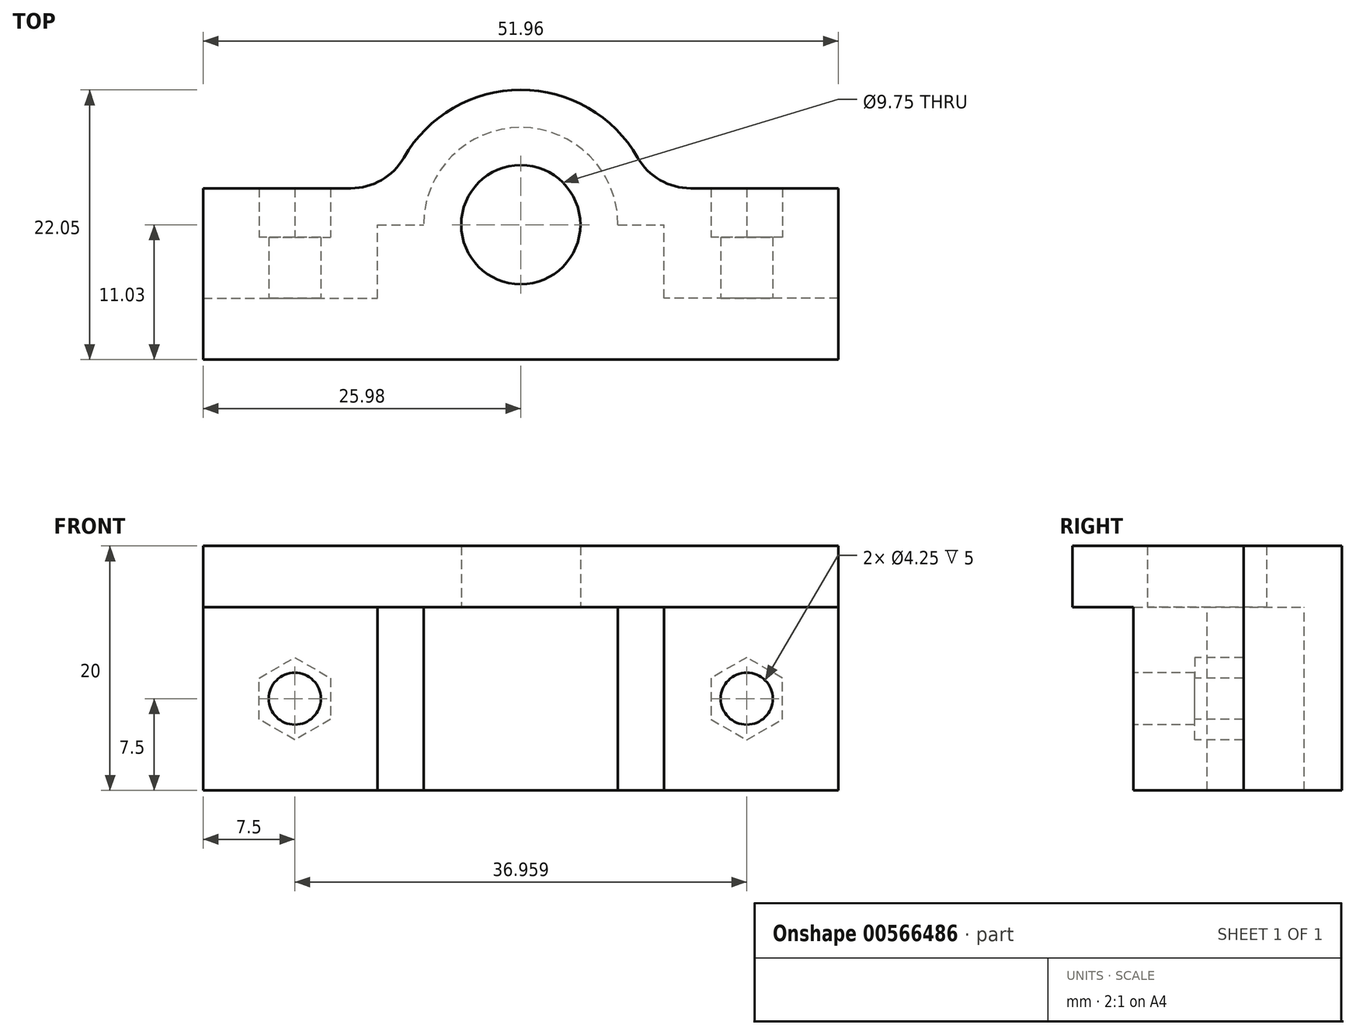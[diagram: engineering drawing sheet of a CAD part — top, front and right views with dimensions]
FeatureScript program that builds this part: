
annotation { "Feature Type Name" : "Feature", "Feature Type Description" : "" }
export const myFeature = defineFeature(function(context is Context, id is Id, definition is map)
    precondition{}
    {
        {
            var Q0;
            Q0=qCreatedBy(makeId("Top.planeOp"),FACE);
            var sketch = newSketch(context, id + "F0", { "sketchPlane" : qUnion([Q0])});
            skCircle(sketch, "E0", {"center": v(0, 0) * mm, "radius": 4.75 * mm});
            skCircle(sketch, "E1", {"center": v(0, 0) * mm, "radius": 7.83 * mm, "construction": true});
            skLineSegment(sketch, "E2", {"start": v(0, -11.03) * mm, "end": v(10.98, -11.03) * mm});
            skLineSegment(sketch, "E3", {"start": v(25.98, -11.03) * mm, "end": v(25.98, -6.02) * mm, "construction": true});
            skLineSegment(sketch, "E4", {"start": v(25.98, -6.02) * mm, "end": v(10.98, -6.03) * mm});
            skLineSegment(sketch, "E5", {"start": v(10.98, -1.03) * mm, "end": v(10.98, 1) * mm});
            skArc(sketch, "E6", {"start": v(10.98, 1) * mm, "mid": v(7.43, 8.14) * mm, "end": v(0, 11.03) * mm});
            skArc(sketch, "E7.MirrorCS", {"start": v(-10.98, 1) * mm, "mid": v(-7.43, 8.14) * mm, "end": v(0, 11.03) * mm});
            skLineSegment(sketch, "E8.MirrorCS", {"start": v(-10.98, -1.02) * mm, "end": v(-10.98, 1) * mm});
            skLineSegment(sketch, "E9.MirrorCS", {"start": v(-25.98, -6.02) * mm, "end": v(-10.98, -6.03) * mm});
            skLineSegment(sketch, "E10.MirrorCS", {"start": v(-25.98, -11.03) * mm, "end": v(-25.98, -6.02) * mm, "construction": true});
            skLineSegment(sketch, "E11.MirrorCS", {"start": v(0, -11.03) * mm, "end": v(-10.98, -11.03) * mm});
            skLineSegment(sketch, "E12", {"start": v(25.98, -6.02) * mm, "end": v(25.98, -1.02) * mm});
            skLineSegment(sketch, "E13", {"start": v(25.98, -1.02) * mm, "end": v(10.98, -1.03) * mm});
            skPoint(sketch, "E13.endSnap0", {"position": v(10.98, -2.51) * mm});
            skLineSegment(sketch, "E14.MirrorCS", {"start": v(-25.98, -1.02) * mm, "end": v(-10.98, -1.03) * mm});
            skLineSegment(sketch, "E15.MirrorCS", {"start": v(-25.98, -6.02) * mm, "end": v(-25.98, -1.02) * mm});
            skPoint(sketch, "E16.orphan", {"position": v(-10.98, -6.03) * mm});
            skLineSegment(sketch, "E17", {"start": v(-10.98, -11.03) * mm, "end": v(-10.98, -6.03) * mm});
            skLineSegment(sketch, "E18.MirrorCS", {"start": v(10.98, -11.03) * mm, "end": v(10.98, -6.03) * mm});
            skPoint(sketch, "E19.orphan", {"position": v(-25.98, -11.03) * mm});
            skSolve(sketch);
        }
        {
            var Q0;
            Q0=qSketchRegion(id+"F0",true);
            extrude(context, id + "F1", {"entities" : qUnion([Q0]), "endBound" : BoundingType.SYMMETRIC, "depth" : 15 * mm});
        }
        {
            var Q0;
            Q0=makeQuery(id+"F1.opExtrude","SWEPT_FACE",FACE,{"disambiguationData":[OSD([sQuery(id+"F0.wireOp",EDGE,"E2"),sQuery(id+"F0.wireOp",EDGE,"E11.MirrorCS")])]});
            var sketch = newSketch(context, id + "F2", { "sketchPlane" : qUnion([Q0])});
            skCircle(sketch, "E20", {"center": v(-18.48, 0) * mm, "radius": 2.12 * mm});
            skCircle(sketch, "E21.MirrorC", {"center": v(18.48, 0) * mm, "radius": 2.12 * mm});
            skSolve(sketch);
        }
        {
            var Q0;
            Q0=qSketchRegion(id+"F2",true);
            extrude(context, id + "F3", {"entities" : qUnion([Q0]), "operationType" : NewBodyOperationType.REMOVE, "oppositeDirection" : true, "depth" : 25 * mm});
        }
        {
            var Q0;
            Q0=makeQuery(id+"F1.opExtrude","CAP_FACE",FACE,{"disambiguationData":[OSD([sQuery(id+"F0.wireOp",EDGE,"E0"),sQuery(id+"F0.wireOp",EDGE,"E2"),sQuery(id+"F0.wireOp",EDGE,"E3"),sQuery(id+"F0.wireOp",EDGE,"E4"),sQuery(id+"F0.wireOp",EDGE,"E5"),sQuery(id+"F0.wireOp",EDGE,"E6"),sQuery(id+"F0.wireOp",EDGE,"E7.MirrorCS"),sQuery(id+"F0.wireOp",EDGE,"E8.MirrorCS"),sQuery(id+"F0.wireOp",EDGE,"E9.MirrorCS"),sQuery(id+"F0.wireOp",EDGE,"E10.MirrorCS"),sQuery(id+"F0.wireOp",EDGE,"E11.MirrorCS")])],"isStart":false});
            var sketch = newSketch(context, id + "F4", { "sketchPlane" : qUnion([Q0])});
            skArc(sketch, "E22", {"start": v(7.82, -0.01) * mm, "mid": v(0, 7.83) * mm, "end": v(-7.82, -0.01) * mm});
            skLineSegment(sketch, "E23.top", {"start": v(-10.98, -11.03) * mm, "end": v(10.98, -11.03) * mm});
            skLineSegment(sketch, "E23.left", {"start": v(-10.98, -6.03) * mm, "end": v(-10.98, -11.03) * mm});
            skLineSegment(sketch, "E23.right", {"start": v(10.98, -6.03) * mm, "end": v(10.98, -11.03) * mm});
            skPoint(sketch, "E24.startSnap0", {"position": v(-10.98, -0.01) * mm});
            skLineSegment(sketch, "E25", {"start": v(-7.82, -0.01) * mm, "end": v(-10.98, -0.01) * mm});
            skLineSegment(sketch, "E26", {"start": v(-10.98, -6.03) * mm, "end": v(-10.98, -0.01) * mm});
            skLineSegment(sketch, "E27.MirrorCS", {"start": v(7.82, -0.01) * mm, "end": v(10.98, -0.01) * mm});
            skLineSegment(sketch, "E28.MirrorCS", {"start": v(10.98, -6.03) * mm, "end": v(10.98, -0.01) * mm});
            skPoint(sketch, "E23.bottom.end.orphan", {"position": v(-7.82, -6.03) * mm});
            skPoint(sketch, "E29.trimOffspring.start.orphan", {"position": v(7.82, -6.03) * mm});
            skSolve(sketch);
        }
        {
            var Q0;
            Q0=qSketchRegion(id+"F4",true);
            extrude(context, id + "F5", {"entities" : qUnion([Q0]), "operationType" : NewBodyOperationType.REMOVE, "endBound" : BoundingType.THROUGH_ALL, "oppositeDirection" : true, "depth" : 10 * mm});
        }
        {
            var Q0;
            Q0=qCreatedBy(makeId("Top.planeOp"),FACE);
            var sketch = newSketch(context, id + "F6", { "sketchPlane" : qUnion([Q0])});
            skLineSegment(sketch, "E30", {"start": v(-10.98, 1) * mm, "end": v(-10.98, -1.03) * mm});
            skLineSegment(sketch, "E31", {"start": v(-10.98, -1.03) * mm, "end": v(-14.18, -1.03) * mm});
            skLineSegment(sketch, "E32", {"start": v(-14.18, -1.03) * mm, "end": v(-14.18, 2.97) * mm});
            skLineSegment(sketch, "E33", {"start": v(-14.18, 2.97) * mm, "end": v(-10.62, 2.97) * mm});
            skArc(sketch, "E34", {"start": v(-10.62, 2.98) * mm, "mid": v(-10.84, 2) * mm, "end": v(-10.98, 1) * mm});
            skArc(sketch, "E35.MirrorCS", {"start": v(10.62, 2.98) * mm, "mid": v(10.84, 2) * mm, "end": v(10.98, 1) * mm});
            skLineSegment(sketch, "E36.MirrorCS", {"start": v(10.98, -1.03) * mm, "end": v(14.18, -1.03) * mm});
            skLineSegment(sketch, "E37.MirrorCS", {"start": v(14.18, 2.98) * mm, "end": v(10.62, 2.97) * mm});
            skLineSegment(sketch, "E38.MirrorCS", {"start": v(10.98, 1) * mm, "end": v(10.98, -1.03) * mm});
            skLineSegment(sketch, "E39.MirrorCS", {"start": v(14.18, -1.03) * mm, "end": v(14.18, 2.97) * mm});
            skSolve(sketch);
        }
        {
            var Q0;
            Q0=qSketchRegion(id+"F6",true);
            extrude(context, id + "F7", {"entities" : qUnion([Q0]), "operationType" : NewBodyOperationType.ADD, "endBound" : BoundingType.SYMMETRIC, "depth" : 15 * mm});
        }
        {
            var Q0;
            {var subQ0=sQuery(id+"F0.wireOp",EDGE,"E9.MirrorCS");var subQ1=sQuery(id+"F0.wireOp",EDGE,"E14.MirrorCS");var subQ2=sQuery(id+"F0.wireOp",EDGE,"E15.MirrorCS");var subQ3=sQuery(id+"F0.wireOp",EDGE,"E13");var subQ4=sQuery(id+"F0.wireOp",EDGE,"E12");var subQ5=sQuery(id+"F0.wireOp",EDGE,"E8.MirrorCS");var subQ6=sQuery(id+"F0.wireOp",EDGE,"E7.MirrorCS");var subQ7=sQuery(id+"F0.wireOp",EDGE,"E6");var subQ8=sQuery(id+"F0.wireOp",EDGE,"E5");var subQ9=sQuery(id+"F0.wireOp",EDGE,"E4");var subQ10=makeQuery(id+"F1.opExtrude","CAP_FACE",FACE,{"disambiguationData":[OSD([sQuery(id+"F0.wireOp",EDGE,"E0"),sQuery(id+"F0.wireOp",EDGE,"E2"),subQ9,subQ8,subQ7,subQ6,subQ5,subQ0,sQuery(id+"F0.wireOp",EDGE,"E11.MirrorCS"),subQ4,subQ3,subQ1,subQ2,sQuery(id+"F0.wireOp",EDGE,"E17"),sQuery(id+"F0.wireOp",EDGE,"E18.MirrorCS")])],"isStart":false});Q0=makeQuery(id+"F7.boolean.opBoolean","MERGE",FACE,{"derivedFrom":[makeQuery(id+"F5.boolean.opBoolean","SPLIT",FACE,{"disambiguationData":[TD([makeQuery(id+"F1.opExtrude","SWEPT_FACE",FACE,{"disambiguationData":[OSD([subQ9])]})])],"derivedFrom":subQ10}),makeQuery(id+"F5.boolean.opBoolean","SPLIT",FACE,{"disambiguationData":[TD([makeQuery(id+"F1.opExtrude","SWEPT_FACE",FACE,{"disambiguationData":[OSD([subQ8])]})])],"derivedFrom":subQ10}),makeQuery(id+"F5.boolean.opBoolean","SPLIT",FACE,{"disambiguationData":[TD([makeQuery(id+"F1.opExtrude","SWEPT_FACE",FACE,{"disambiguationData":[OSD([subQ0])]})])],"derivedFrom":subQ10}),makeQuery(id+"F7.opExtrude","CAP_FACE",FACE,{"disambiguationData":[OSD([sQuery(id+"F6.wireOp",EDGE,"E30"),sQuery(id+"F6.wireOp",EDGE,"E31"),sQuery(id+"F6.wireOp",EDGE,"E32"),sQuery(id+"F6.wireOp",EDGE,"E33"),sQuery(id+"F6.wireOp",EDGE,"E34")])],"isStart":false}),makeQuery(id+"F7.opExtrude","CAP_FACE",FACE,{"disambiguationData":[OSD([sQuery(id+"F6.wireOp",EDGE,"E35.MirrorCS"),sQuery(id+"F6.wireOp",EDGE,"E36.MirrorCS"),sQuery(id+"F6.wireOp",EDGE,"E37.MirrorCS"),sQuery(id+"F6.wireOp",EDGE,"E38.MirrorCS"),sQuery(id+"F6.wireOp",EDGE,"E39.MirrorCS")])],"isStart":false})]});}
            var sketch = newSketch(context, id + "F8", { "sketchPlane" : qUnion([Q0])});
            skLineSegment(sketch, "E40", {"start": v(-10.98, -6.02) * mm, "end": v(-25.98, -6.02) * mm});
            skLineSegment(sketch, "E41", {"start": v(-25.98, -6.02) * mm, "end": v(-25.98, -1.02) * mm});
            skLineSegment(sketch, "E42", {"start": v(-25.98, -1.02) * mm, "end": v(-14.18, -1.03) * mm});
            skLineSegment(sketch, "E43", {"start": v(-14.18, -1.03) * mm, "end": v(-14.18, 2.98) * mm});
            skLineSegment(sketch, "E44", {"start": v(-14.18, 2.97) * mm, "end": v(-10.62, 2.97) * mm});
            skArc(sketch, "E45", {"start": v(-10.62, 2.97) * mm, "mid": v(0, 11.03) * mm, "end": v(10.62, 2.98) * mm});
            skLineSegment(sketch, "E46.MirrorCS", {"start": v(14.18, 2.98) * mm, "end": v(10.62, 2.98) * mm});
            skLineSegment(sketch, "E47.MirrorCS", {"start": v(14.18, -1.03) * mm, "end": v(14.18, 2.98) * mm});
            skLineSegment(sketch, "E48.MirrorCS", {"start": v(25.98, -1.02) * mm, "end": v(14.18, -1.03) * mm});
            skLineSegment(sketch, "E49.MirrorCS", {"start": v(25.98, -6.02) * mm, "end": v(25.98, -1.02) * mm});
            skLineSegment(sketch, "E50.MirrorCS", {"start": v(10.98, -6.02) * mm, "end": v(25.98, -6.02) * mm});
            skLineSegment(sketch, "E51", {"start": v(-10.98, -6.02) * mm, "end": v(10.98, -6.02) * mm});
            skCircle(sketch, "E52", {"center": v(0, 0) * mm, "radius": 4.88 * mm});
            skSolve(sketch);
        }
        {
            var Q0;
            Q0=qSketchRegion(id+"F8",true);
            extrude(context, id + "F9", {"entities" : qUnion([Q0]), "operationType" : NewBodyOperationType.ADD, "depth" : 5 * mm});
        }
        {
            var Q0;
            Q0=makeQuery(id+"F9.boolean.opBoolean","MERGE",FACE,{"derivedFrom":[makeQuery(id+"F1.opExtrude","SWEPT_FACE",FACE,{"disambiguationData":[OSD([sQuery(id+"F0.wireOp",EDGE,"E4")])]}),makeQuery(id+"F1.opExtrude","SWEPT_FACE",FACE,{"disambiguationData":[OSD([sQuery(id+"F0.wireOp",EDGE,"E9.MirrorCS")])]}),makeQuery(id+"F9.opExtrude","SWEPT_FACE",FACE,{"disambiguationData":[OSD([sQuery(id+"F8.wireOp",EDGE,"E40"),sQuery(id+"F8.wireOp",EDGE,"E50.MirrorCS"),sQuery(id+"F8.wireOp",EDGE,"E51")])]})]});
            var sketch = newSketch(context, id + "F10", { "sketchPlane" : qUnion([Q0])});
            skLineSegment(sketch, "E53.bottom", {"start": v(-25.98, 12.5) * mm, "end": v(25.98, 12.5) * mm});
            skLineSegment(sketch, "E53.top", {"start": v(-25.98, 7.5) * mm, "end": v(25.98, 7.5) * mm});
            skLineSegment(sketch, "E53.left", {"start": v(-25.98, 12.5) * mm, "end": v(-25.98, 7.5) * mm});
            skLineSegment(sketch, "E53.right", {"start": v(25.98, 12.5) * mm, "end": v(25.98, 7.5) * mm});
            skSolve(sketch);
        }
        {
            var Q0;
            Q0=qSketchRegion(id+"F10",true);
            extrude(context, id + "F11", {"entities" : qUnion([Q0]), "operationType" : NewBodyOperationType.ADD, "depth" : 5 * mm});
        }
        {
            var Q0;
            Q0=makeQuery(id+"F9.boolean.opBoolean","MERGE",FACE,{"derivedFrom":[makeQuery(id+"F1.opExtrude","SWEPT_FACE",FACE,{"disambiguationData":[OSD([sQuery(id+"F0.wireOp",EDGE,"E13")])]}),makeQuery(id+"F9.opExtrude","SWEPT_FACE",FACE,{"disambiguationData":[OSD([sQuery(id+"F8.wireOp",EDGE,"E48.MirrorCS")])]})]});
            var sketch = newSketch(context, id + "F12", { "sketchPlane" : qUnion([Q0])});
            skCircle(sketch, "E54.cCircle", {"center": v(-18.48, 0) * mm, "radius": 2.93 * mm, "construction": true});
            skLineSegment(sketch, "E54.0", {"start": v(-15.55, 1.69) * mm, "end": v(-15.55, -1.69) * mm});
            skLineSegment(sketch, "E54.1", {"start": v(-15.55, -1.69) * mm, "end": v(-18.48, -3.38) * mm});
            skLineSegment(sketch, "E54.2", {"start": v(-18.48, -3.38) * mm, "end": v(-21.4, -1.69) * mm});
            skLineSegment(sketch, "E54.3", {"start": v(-21.4, -1.69) * mm, "end": v(-21.4, 1.69) * mm});
            skLineSegment(sketch, "E54.4", {"start": v(-21.4, 1.69) * mm, "end": v(-18.48, 3.38) * mm});
            skLineSegment(sketch, "E54.5", {"start": v(-18.48, 3.38) * mm, "end": v(-15.55, 1.69) * mm});
            skPoint(sketch, "E54.0.midPoint", {"position": v(-15.55, 0) * mm});
            skLineSegment(sketch, "E55.MirrorCS", {"start": v(18.48, 3.38) * mm, "end": v(15.55, 1.69) * mm});
            skLineSegment(sketch, "E56.MirrorCS", {"start": v(21.4, 1.69) * mm, "end": v(18.48, 3.38) * mm});
            skLineSegment(sketch, "E57.MirrorCS", {"start": v(21.4, -1.69) * mm, "end": v(21.4, 1.69) * mm});
            skLineSegment(sketch, "E58.MirrorCS", {"start": v(18.48, -3.38) * mm, "end": v(21.4, -1.69) * mm});
            skLineSegment(sketch, "E59.MirrorCS", {"start": v(15.55, -1.69) * mm, "end": v(18.48, -3.38) * mm});
            skLineSegment(sketch, "E60.MirrorCS", {"start": v(15.55, 1.69) * mm, "end": v(15.55, -1.69) * mm});
            skPoint(sketch, "E61.MirrorP", {"position": v(15.55, 0) * mm});
            skCircle(sketch, "E62.MirrorC", {"center": v(18.48, 0) * mm, "radius": 2.93 * mm, "construction": true});
            skLineSegment(sketch, "E63.bottom", {"start": v(-25.98, 12.5) * mm, "end": v(-14.18, 12.5) * mm});
            skLineSegment(sketch, "E63.top", {"start": v(-25.98, -7.5) * mm, "end": v(-14.18, -7.5) * mm});
            skLineSegment(sketch, "E63.left", {"start": v(-25.98, 12.5) * mm, "end": v(-25.98, -7.5) * mm});
            skLineSegment(sketch, "E63.right", {"start": v(-14.18, 12.5) * mm, "end": v(-14.18, -7.5) * mm});
            skLineSegment(sketch, "E64.MirrorCS", {"start": v(14.18, 12.5) * mm, "end": v(14.18, -7.5) * mm});
            skLineSegment(sketch, "E65.MirrorCS", {"start": v(25.98, 12.5) * mm, "end": v(14.18, 12.5) * mm});
            skLineSegment(sketch, "E66.MirrorCS", {"start": v(25.98, 12.5) * mm, "end": v(25.98, -7.5) * mm});
            skLineSegment(sketch, "E67.MirrorCS", {"start": v(25.98, -7.5) * mm, "end": v(14.18, -7.5) * mm});
            skSolve(sketch);
        }
        {
            var Q0;
            Q0=qSketchRegion(id+"F12",true);
            extrude(context, id + "F13", {"entities" : qUnion([Q0]), "operationType" : NewBodyOperationType.ADD, "depth" : 4 * mm});
        }
        {
            var Q0;
            Q0=makeQuery(id+"F9.boolean.opBoolean","MERGE",EDGE,{"derivedFrom":[makeQuery(id+"F7.opExtrude","SWEPT_EDGE",EDGE,{"disambiguationData":[OSD([sQuery(id+"F6.wireOp",EDGE,"E35.MirrorCS"),sQuery(id+"F6.wireOp",EDGE,"E37.MirrorCS")])]}),makeQuery(id+"F9.opExtrude","SWEPT_EDGE",EDGE,{"disambiguationData":[OSD([sQuery(id+"F8.wireOp",EDGE,"E45"),sQuery(id+"F8.wireOp",EDGE,"E46.MirrorCS")])]})]});
            var Q1;
            Q1=makeQuery(id+"F9.boolean.opBoolean","MERGE",EDGE,{"derivedFrom":[makeQuery(id+"F7.opExtrude","SWEPT_EDGE",EDGE,{"disambiguationData":[OSD([sQuery(id+"F6.wireOp",EDGE,"E33"),sQuery(id+"F6.wireOp",EDGE,"E34")])]}),makeQuery(id+"F9.opExtrude","SWEPT_EDGE",EDGE,{"disambiguationData":[OSD([sQuery(id+"F8.wireOp",EDGE,"E44"),sQuery(id+"F8.wireOp",EDGE,"E45")])]})]});
            fillet(context, id + "F14", {"entities" : qUnion([Q0, Q1]), "radius" : 5 * mm, "tangentPropagation" : true, "allowEdgeOverflow" : false});
        }
        {
            var Q0;
            Q0=makeQuery(id+"F11.boolean.opBoolean","MERGE",FACE,{"derivedFrom":[makeQuery(id+"F9.opExtrude","CAP_FACE",FACE,{"disambiguationData":[OSD([sQuery(id+"F8.wireOp",EDGE,"E40"),sQuery(id+"F8.wireOp",EDGE,"E41"),sQuery(id+"F8.wireOp",EDGE,"E42"),sQuery(id+"F8.wireOp",EDGE,"E43"),sQuery(id+"F8.wireOp",EDGE,"E44"),sQuery(id+"F8.wireOp",EDGE,"E45"),sQuery(id+"F8.wireOp",EDGE,"E46.MirrorCS"),sQuery(id+"F8.wireOp",EDGE,"E47.MirrorCS"),sQuery(id+"F8.wireOp",EDGE,"E48.MirrorCS"),sQuery(id+"F8.wireOp",EDGE,"E49.MirrorCS"),sQuery(id+"F8.wireOp",EDGE,"E50.MirrorCS"),sQuery(id+"F8.wireOp",EDGE,"E51"),sQuery(id+"F8.wireOp",EDGE,"E52")])],"isStart":true}),makeQuery(id+"F11.opExtrude","SWEPT_FACE",FACE,{"disambiguationData":[OSD([sQuery(id+"F10.wireOp",EDGE,"E53.top")])]})]});
            var sketch = newSketch(context, id + "F15", { "sketchPlane" : qUnion([Q0])});
            skLineSegment(sketch, "E68.bottom", {"start": v(-11.73, 6.03) * mm, "end": v(11.73, 6.03) * mm});
            skLineSegment(sketch, "E68.top", {"start": v(-11.73, 0) * mm, "end": v(-7.95, 0) * mm});
            skLineSegment(sketch, "E68.left", {"start": v(-11.73, 6.03) * mm, "end": v(-11.73, 0) * mm});
            skLineSegment(sketch, "E68.right", {"start": v(11.73, 6.03) * mm, "end": v(11.73, 0) * mm});
            skArc(sketch, "E69", {"start": v(-7.95, 0.01) * mm, "mid": v(0, -7.95) * mm, "end": v(7.95, 0) * mm});
            skLineSegment(sketch, "E70.trimOffspring", {"start": v(7.95, 0) * mm, "end": v(11.73, 0) * mm});
            skSolve(sketch);
        }
        {
            var Q0;
            Q0=qSketchRegion(id+"F15",true);
            extrude(context, id + "F16", {"entities" : qUnion([Q0]), "operationType" : NewBodyOperationType.REMOVE, "depth" : 25 * mm});
        }
    });
